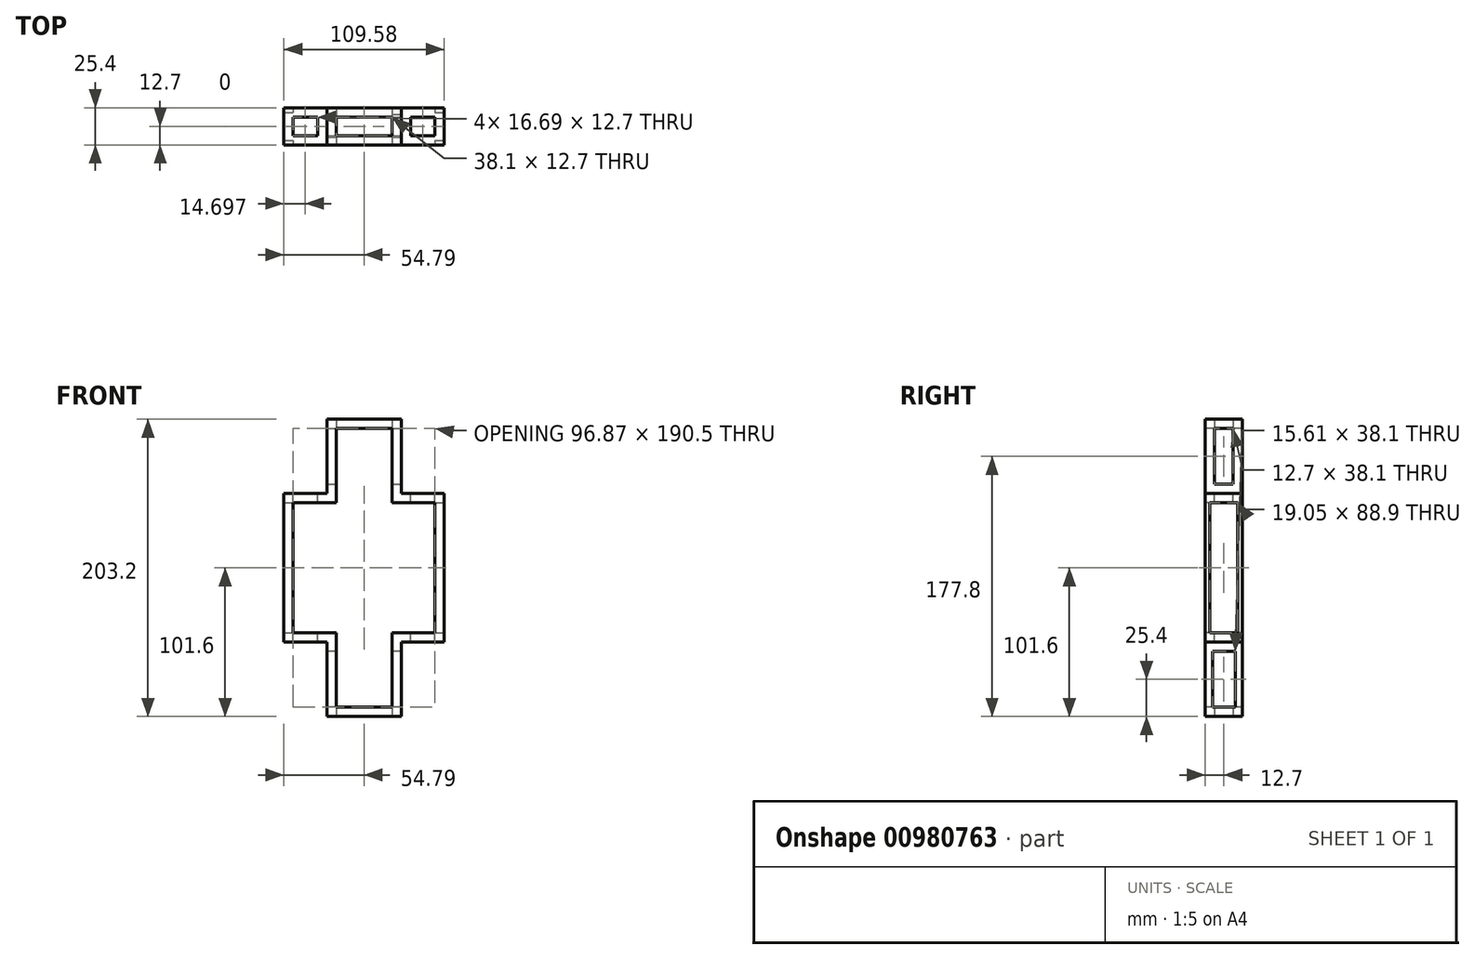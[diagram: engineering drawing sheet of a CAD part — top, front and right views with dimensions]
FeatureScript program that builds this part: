
annotation { "Feature Type Name" : "Feature", "Feature Type Description" : "" }
export const myFeature = defineFeature(function(context is Context, id is Id, definition is map)
    precondition{}
    {
        {
            var Q0;
            Q0=qCreatedBy(makeId("Front.planeOp"),FACE);
            var sketch = newSketch(context, id + "F0", { "sketchPlane" : qUnion([Q0])});
            skLineSegment(sketch, "E0", {"start": v(0, 141.5) * mm, "end": v(0, -155.81) * mm, "construction": true});
            skLineSegment(sketch, "E1", {"start": v(0, 101.6) * mm, "end": v(25.4, 101.6) * mm});
            skLineSegment(sketch, "E2", {"start": v(25.4, 101.6) * mm, "end": v(25.4, 50.8) * mm});
            skLineSegment(sketch, "E3", {"start": v(25.4, 50.8) * mm, "end": v(54.79, 50.8) * mm});
            skLineSegment(sketch, "E4", {"start": v(54.79, 50.8) * mm, "end": v(54.79, -50.8) * mm});
            skLineSegment(sketch, "E5", {"start": v(54.79, -50.8) * mm, "end": v(25.4, -50.8) * mm});
            skLineSegment(sketch, "E6", {"start": v(25.4, -50.8) * mm, "end": v(25.4, -101.6) * mm});
            skLineSegment(sketch, "E7", {"start": v(25.4, -101.6) * mm, "end": v(0, -101.6) * mm});
            skLineSegment(sketch, "E8", {"start": v(-105.83, 0) * mm, "end": v(123.44, 0) * mm, "construction": true});
            skPoint(sketch, "E9", {"position": v(54.79, 0) * mm});
            skLineSegment(sketch, "E10.MirrorCS", {"start": v(0, 101.6) * mm, "end": v(-25.4, 101.6) * mm});
            skLineSegment(sketch, "E11.MirrorCS", {"start": v(-25.4, 101.6) * mm, "end": v(-25.4, 50.8) * mm});
            skLineSegment(sketch, "E12.MirrorCS", {"start": v(-25.4, 50.8) * mm, "end": v(-54.79, 50.8) * mm});
            skLineSegment(sketch, "E13.MirrorCS", {"start": v(-54.79, 50.8) * mm, "end": v(-54.79, -50.8) * mm});
            skLineSegment(sketch, "E14.MirrorCS", {"start": v(-54.79, -50.8) * mm, "end": v(-25.4, -50.8) * mm});
            skLineSegment(sketch, "E15.MirrorCS", {"start": v(-25.4, -50.8) * mm, "end": v(-25.4, -101.6) * mm});
            skLineSegment(sketch, "E16.MirrorCS", {"start": v(-25.4, -101.6) * mm, "end": v(0, -101.6) * mm});
            skPoint(sketch, "E17.orphan", {"position": v(0, 82.16) * mm});
            skSolve(sketch);
        }
        {
            var Q0;
            Q0=makeQuery(id+"F0.imprint","IMPRINT",FACE,{"disambiguationData":[TD([[makeQuery(id+"F0.imprint","IMPRINT",EDGE,{"derivedFrom":sQuery(id+"F0.wireOp",EDGE,"E1")}),-1.0]])]});
            extrude(context, id + "F1", {"entities" : qUnion([Q0]), "endBound" : BoundingType.SYMMETRIC, "depth" : 25.4 * mm, "offsetDistance" : 25.4 * mm});
        }
        {
            var Q0;
            Q0=makeQuery(id+"F1.opExtrude","SWEPT_FACE",FACE,{"disambiguationData":[OSD([sQuery(id+"F0.wireOp",EDGE,"E4")])]});
            var sketch = newSketch(context, id + "F2", { "sketchPlane" : qUnion([Q0])});
            skLineSegment(sketch, "E18.bottom", {"start": v(9.53, -44.45) * mm, "end": v(-9.53, -44.45) * mm});
            skLineSegment(sketch, "E18.top", {"start": v(9.53, 44.45) * mm, "end": v(-9.53, 44.45) * mm});
            skLineSegment(sketch, "E18.left", {"start": v(9.53, -44.45) * mm, "end": v(9.53, 44.45) * mm});
            skLineSegment(sketch, "E18.right", {"start": v(-9.53, -44.45) * mm, "end": v(-9.53, 44.45) * mm});
            skPoint(sketch, "E18.middle", {"position": v(0, 0) * mm});
            skSolve(sketch);
        }
        {
            var Q0;
            Q0=makeQuery(id+"F2.imprint","IMPRINT",FACE,{"disambiguationData":[TD([[makeQuery(id+"F2.imprint","IMPRINT",EDGE,{"derivedFrom":sQuery(id+"F2.wireOp",EDGE,"E18.bottom")}),-1.0]])]});
            extrude(context, id + "F3", {"entities" : qUnion([Q0]), "operationType" : NewBodyOperationType.REMOVE, "endBound" : BoundingType.THROUGH_ALL, "oppositeDirection" : true, "depth" : 25.4 * mm, "offsetDistance" : 25.4 * mm});
        }
        {
            var Q0;
            Q0=makeQuery(id+"F1.opExtrude","SWEPT_FACE",FACE,{"disambiguationData":[OSD([sQuery(id+"F0.wireOp",EDGE,"E7"),sQuery(id+"F0.wireOp",EDGE,"E16.MirrorCS")])]});
            var sketch = newSketch(context, id + "F4", { "sketchPlane" : qUnion([Q0])});
            skLineSegment(sketch, "E19.bottom", {"start": v(-19.05, -6.35) * mm, "end": v(19.05, -6.35) * mm});
            skLineSegment(sketch, "E19.top", {"start": v(-19.05, 6.35) * mm, "end": v(19.05, 6.35) * mm});
            skLineSegment(sketch, "E19.left", {"start": v(-19.05, -6.35) * mm, "end": v(-19.05, 6.35) * mm});
            skLineSegment(sketch, "E19.right", {"start": v(19.05, -6.35) * mm, "end": v(19.05, 6.35) * mm});
            skPoint(sketch, "E19.middle", {"position": v(0, 0) * mm});
            skSolve(sketch);
        }
        {
            var Q0;
            Q0=makeQuery(id+"F4.imprint","IMPRINT",FACE,{"disambiguationData":[TD([[makeQuery(id+"F4.imprint","IMPRINT",EDGE,{"derivedFrom":sQuery(id+"F4.wireOp",EDGE,"E19.bottom")}),1.0]])]});
            extrude(context, id + "F5", {"entities" : qUnion([Q0]), "operationType" : NewBodyOperationType.REMOVE, "endBound" : BoundingType.THROUGH_ALL, "oppositeDirection" : true, "depth" : 25.4 * mm, "offsetDistance" : 25.4 * mm});
        }
        {
            var Q0;
            Q0=makeQuery(id+"F1.opExtrude","SWEPT_FACE",FACE,{"disambiguationData":[OSD([sQuery(id+"F0.wireOp",EDGE,"E2")])]});
            var sketch = newSketch(context, id + "F6", { "sketchPlane" : qUnion([Q0])});
            skPoint(sketch, "E20", {"position": v(0, 76.2) * mm});
            skPoint(sketch, "E20.positionSnap0", {"position": v(12.7, 76.2) * mm});
            skLineSegment(sketch, "E21.bottom", {"start": v(-6.35, 95.25) * mm, "end": v(6.35, 95.25) * mm});
            skLineSegment(sketch, "E21.top", {"start": v(-6.35, 57.15) * mm, "end": v(6.35, 57.15) * mm});
            skLineSegment(sketch, "E21.left", {"start": v(-6.35, 95.25) * mm, "end": v(-6.35, 57.15) * mm});
            skLineSegment(sketch, "E21.right", {"start": v(6.35, 95.25) * mm, "end": v(6.35, 57.15) * mm});
            skSolve(sketch);
        }
        {
            var Q0;
            Q0=makeQuery(id+"F6.imprint","IMPRINT",FACE,{"disambiguationData":[TD([[makeQuery(id+"F6.imprint","IMPRINT",EDGE,{"derivedFrom":sQuery(id+"F6.wireOp",EDGE,"E21.bottom")}),-1.0]])]});
            extrude(context, id + "F7", {"entities" : qUnion([Q0]), "operationType" : NewBodyOperationType.REMOVE, "endBound" : BoundingType.THROUGH_ALL, "oppositeDirection" : true, "depth" : 25.4 * mm, "offsetDistance" : 25.4 * mm});
        }
        {
            var Q0;
            Q0=makeQuery(id+"F1.opExtrude","SWEPT_FACE",FACE,{"disambiguationData":[OSD([sQuery(id+"F0.wireOp",EDGE,"E15.MirrorCS")])]});
            var sketch = newSketch(context, id + "F8", { "sketchPlane" : qUnion([Q0])});
            skPoint(sketch, "E22", {"position": v(0, -76.2) * mm});
            skPoint(sketch, "E22.positionSnap0", {"position": v(-12.7, -76.2) * mm});
            skLineSegment(sketch, "E23.bottom", {"start": v(7.8, -95.25) * mm, "end": v(-7.8, -95.25) * mm});
            skLineSegment(sketch, "E23.top", {"start": v(7.8, -57.15) * mm, "end": v(-7.8, -57.15) * mm});
            skLineSegment(sketch, "E23.left", {"start": v(7.8, -95.25) * mm, "end": v(7.8, -57.15) * mm});
            skLineSegment(sketch, "E23.right", {"start": v(-7.8, -95.25) * mm, "end": v(-7.8, -57.15) * mm});
            skSolve(sketch);
        }
        {
            var Q0;
            Q0=makeQuery(id+"F8.imprint","IMPRINT",FACE,{"disambiguationData":[TD([[makeQuery(id+"F8.imprint","IMPRINT",EDGE,{"derivedFrom":sQuery(id+"F8.wireOp",EDGE,"E23.bottom")}),-1.0]])]});
            extrude(context, id + "F9", {"entities" : qUnion([Q0]), "operationType" : NewBodyOperationType.REMOVE, "endBound" : BoundingType.THROUGH_ALL, "oppositeDirection" : true, "depth" : 25.4 * mm, "offsetDistance" : 25.4 * mm});
        }
        {
            var Q0;
            Q0=makeQuery(id+"F1.opExtrude","CAP_FACE",FACE,{"disambiguationData":[OSD([sQuery(id+"F0.wireOp",EDGE,"E1"),sQuery(id+"F0.wireOp",EDGE,"E2"),sQuery(id+"F0.wireOp",EDGE,"E3"),sQuery(id+"F0.wireOp",EDGE,"E4"),sQuery(id+"F0.wireOp",EDGE,"E5"),sQuery(id+"F0.wireOp",EDGE,"E6"),sQuery(id+"F0.wireOp",EDGE,"E7"),sQuery(id+"F0.wireOp",EDGE,"E10.MirrorCS"),sQuery(id+"F0.wireOp",EDGE,"E11.MirrorCS"),sQuery(id+"F0.wireOp",EDGE,"E12.MirrorCS"),sQuery(id+"F0.wireOp",EDGE,"E13.MirrorCS"),sQuery(id+"F0.wireOp",EDGE,"E14.MirrorCS"),sQuery(id+"F0.wireOp",EDGE,"E15.MirrorCS"),sQuery(id+"F0.wireOp",EDGE,"E16.MirrorCS")])],"isStart":false});
            var sketch = newSketch(context, id + "F10", { "sketchPlane" : qUnion([Q0])});
            skLineSegment(sketch, "E24.bottom", {"start": v(-19.05, 95.25) * mm, "end": v(19.05, 95.25) * mm});
            skLineSegment(sketch, "E24.top", {"start": v(-19.05, -95.25) * mm, "end": v(19.05, -95.25) * mm});
            skLineSegment(sketch, "E24.left", {"start": v(-19.05, 95.25) * mm, "end": v(-19.05, 44.45) * mm});
            skLineSegment(sketch, "E24.right", {"start": v(19.05, 95.25) * mm, "end": v(19.05, 44.45) * mm});
            skPoint(sketch, "E24.middle", {"position": v(0, 0) * mm});
            skLineSegment(sketch, "E25.bottom", {"start": v(-48.44, 44.45) * mm, "end": v(-19.05, 44.45) * mm});
            skLineSegment(sketch, "E25.top", {"start": v(-48.44, -44.45) * mm, "end": v(-19.05, -44.45) * mm});
            skLineSegment(sketch, "E25.left", {"start": v(-48.44, 44.45) * mm, "end": v(-48.44, -44.45) * mm});
            skLineSegment(sketch, "E25.right", {"start": v(48.44, 44.45) * mm, "end": v(48.44, -44.45) * mm});
            skLineSegment(sketch, "E26.trimOffspring", {"start": v(-19.05, -44.45) * mm, "end": v(-19.05, -95.25) * mm});
            skLineSegment(sketch, "E27.trimOffspring", {"start": v(19.05, -44.45) * mm, "end": v(19.05, -95.25) * mm});
            skLineSegment(sketch, "E28.trimOffspring", {"start": v(19.05, 44.45) * mm, "end": v(48.44, 44.45) * mm});
            skLineSegment(sketch, "E29.trimOffspring", {"start": v(19.05, -44.45) * mm, "end": v(48.44, -44.45) * mm});
            skSolve(sketch);
        }
        {
            var Q0;
            Q0=makeQuery(id+"F10.imprint","IMPRINT",FACE,{"disambiguationData":[TD([[makeQuery(id+"F10.imprint","IMPRINT",EDGE,{"derivedFrom":sQuery(id+"F10.wireOp",EDGE,"E24.bottom")}),-1.0]])]});
            extrude(context, id + "F11", {"entities" : qUnion([Q0]), "operationType" : NewBodyOperationType.REMOVE, "endBound" : BoundingType.THROUGH_ALL, "oppositeDirection" : true, "depth" : 25.4 * mm, "offsetDistance" : 25.4 * mm});
        }
        {
            var Q0;
            Q0=makeQuery(id+"F1.opExtrude","SWEPT_FACE",FACE,{"disambiguationData":[OSD([sQuery(id+"F0.wireOp",EDGE,"E12.MirrorCS")])]});
            var sketch = newSketch(context, id + "F12", { "sketchPlane" : qUnion([Q0])});
            skPoint(sketch, "E30", {"position": v(-40.1, 0) * mm});
            skPoint(sketch, "E30.positionSnap0", {"position": v(-40.1, -12.7) * mm});
            skLineSegment(sketch, "E31.bottom", {"start": v(-48.44, -6.35) * mm, "end": v(-31.75, -6.35) * mm});
            skLineSegment(sketch, "E31.top", {"start": v(-48.44, 6.35) * mm, "end": v(-31.75, 6.35) * mm});
            skLineSegment(sketch, "E31.left", {"start": v(-48.44, -6.35) * mm, "end": v(-48.44, 6.35) * mm});
            skLineSegment(sketch, "E31.right", {"start": v(-31.75, -6.35) * mm, "end": v(-31.75, 6.35) * mm});
            skSolve(sketch);
        }
        {
            var Q0;
            Q0=makeQuery(id+"F12.imprint","IMPRINT",FACE,{"disambiguationData":[TD([[makeQuery(id+"F12.imprint","IMPRINT",EDGE,{"derivedFrom":sQuery(id+"F12.wireOp",EDGE,"E31.bottom")}),1.0]])]});
            extrude(context, id + "F13", {"entities" : qUnion([Q0]), "operationType" : NewBodyOperationType.REMOVE, "endBound" : BoundingType.THROUGH_ALL, "oppositeDirection" : true, "depth" : 25.4 * mm, "offsetDistance" : 25.4 * mm});
        }
        {
            var Q0;
            Q0=makeQuery(id+"F1.opExtrude","SWEPT_FACE",FACE,{"disambiguationData":[OSD([sQuery(id+"F0.wireOp",EDGE,"E3")])]});
            var sketch = newSketch(context, id + "F14", { "sketchPlane" : qUnion([Q0])});
            skPoint(sketch, "E32", {"position": v(40.1, 0) * mm});
            skPoint(sketch, "E32.positionSnap0", {"position": v(40.1, 12.7) * mm});
            skLineSegment(sketch, "E33.bottom", {"start": v(48.44, -6.35) * mm, "end": v(31.75, -6.35) * mm});
            skLineSegment(sketch, "E33.top", {"start": v(48.44, 6.35) * mm, "end": v(31.75, 6.35) * mm});
            skLineSegment(sketch, "E33.left", {"start": v(48.44, -6.35) * mm, "end": v(48.44, 6.35) * mm});
            skLineSegment(sketch, "E33.right", {"start": v(31.75, -6.35) * mm, "end": v(31.75, 6.35) * mm});
            skSolve(sketch);
        }
        {
            var Q0;
            Q0=makeQuery(id+"F14.imprint","IMPRINT",FACE,{"disambiguationData":[TD([[makeQuery(id+"F14.imprint","IMPRINT",EDGE,{"derivedFrom":sQuery(id+"F14.wireOp",EDGE,"E33.bottom")}),-1.0]])]});
            extrude(context, id + "F15", {"entities" : qUnion([Q0]), "operationType" : NewBodyOperationType.REMOVE, "endBound" : BoundingType.THROUGH_ALL, "oppositeDirection" : true, "depth" : 25.4 * mm, "offsetDistance" : 25.4 * mm});
        }
    });
